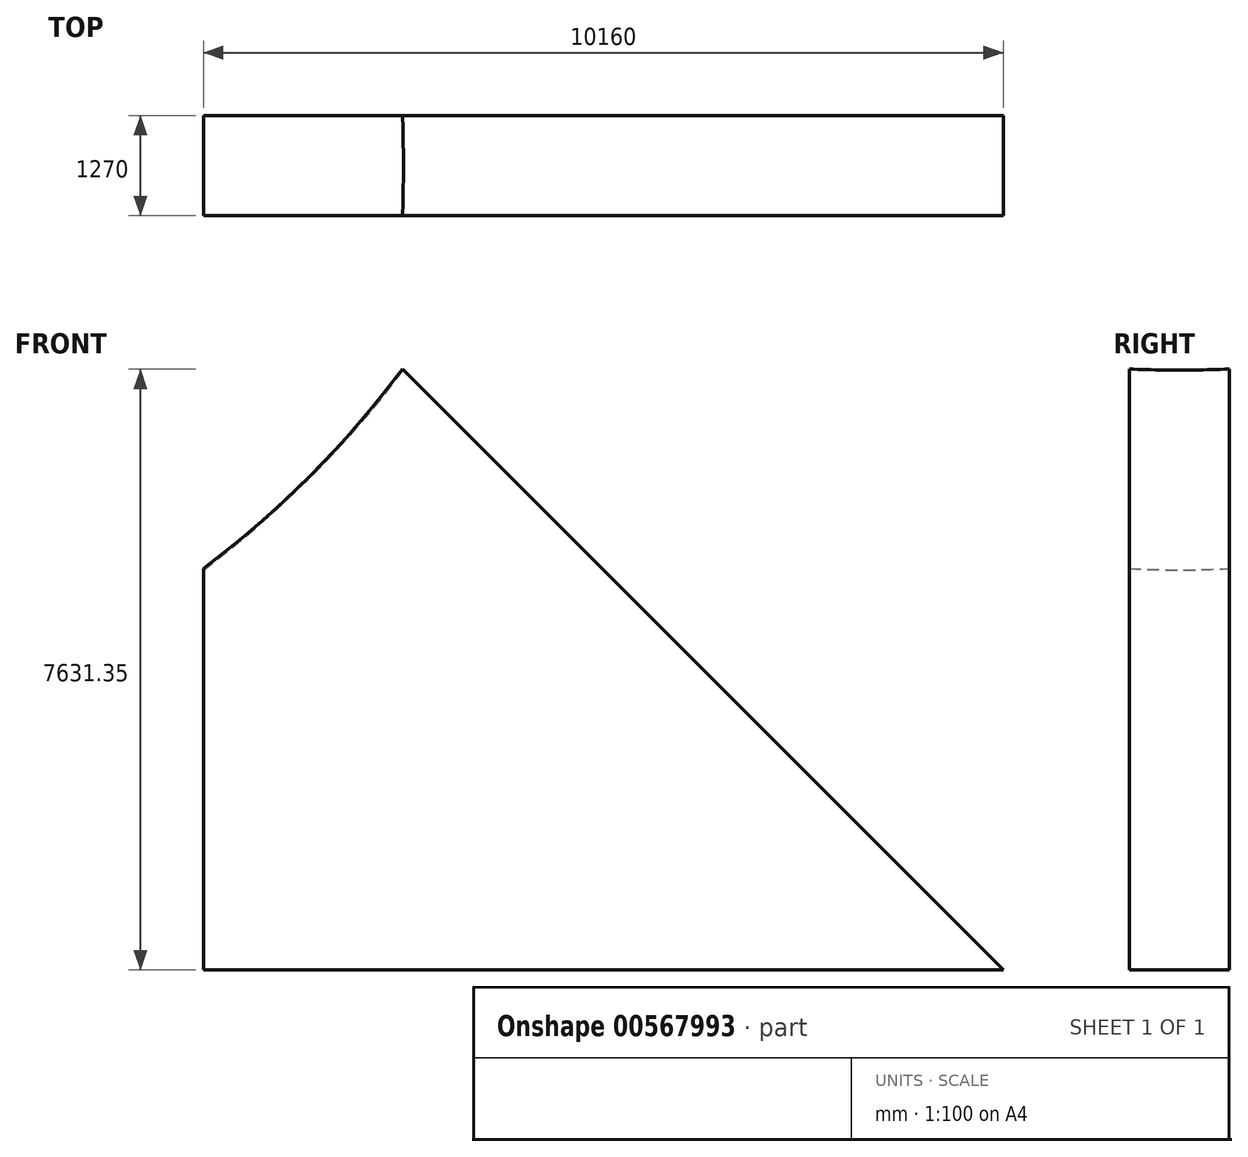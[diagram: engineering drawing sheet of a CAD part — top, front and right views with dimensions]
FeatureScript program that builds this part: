
annotation { "Feature Type Name" : "Feature", "Feature Type Description" : "" }
export const myFeature = defineFeature(function(context is Context, id is Id, definition is map)
    precondition{}
    {
        {
            var Q0;
            Q0=qCreatedBy(makeId("Front.planeOp"),FACE);
            var sketch = newSketch(context, id + "F0", { "sketchPlane" : qUnion([Q0])});
            skLineSegment(sketch, "E0", {"start": v(0, 0) * mm, "end": v(10160, 0) * mm});
            skLineSegment(sketch, "E1", {"start": v(10160, 0) * mm, "end": v(0, 10160) * mm});
            skLineSegment(sketch, "E2", {"start": v(0, 10160) * mm, "end": v(0, 0) * mm});
            skSolve(sketch);
        }
        {
            var Q0;
            Q0=qSketchRegion(id+"F0",true);
            extrude(context, id + "F1", {"entities" : qUnion([Q0]), "endBound" : BoundingType.SYMMETRIC, "depth" : 1270 * mm, "offsetDistance" : 25.4 * mm});
        }
        {
            var Q0;
            Q0=qCreatedBy(makeId("Front.planeOp"),FACE);
            var sketch = newSketch(context, id + "F2", { "sketchPlane" : qUnion([Q0])});
            skArc(sketch, "E3", {"start": v(-20320, 15240) * mm, "mid": v(-7620, 2540) * mm, "end": v(5080, 15240) * mm});
            skLineSegment(sketch, "E4", {"start": v(5080, 15240) * mm, "end": v(-20320, 15240) * mm});
            skLineSegment(sketch, "E5", {"start": v(-7620, 15240) * mm, "end": v(13626.1, 15240) * mm, "construction": true});
            skSolve(sketch);
        }
        {
            var Q0;
            Q0=makeQuery(id+"F2.imprint","IMPRINT",FACE,{"disambiguationData":[TD([[makeQuery(id+"F2.imprint","IMPRINT",EDGE,{"derivedFrom":sQuery(id+"F2.wireOp",EDGE,"E3")}),1.0]])]});
            var Q1;
            Q1=sQuery(id+"F2.wireOp",EDGE,"E5");
            revolve(context, id + "F3", {"operationType" : NewBodyOperationType.REMOVE, "entities" : qUnion([Q0]), "axis" : qUnion([Q1]), "revolveType" : RevolveType.FULL});
        }
    });
